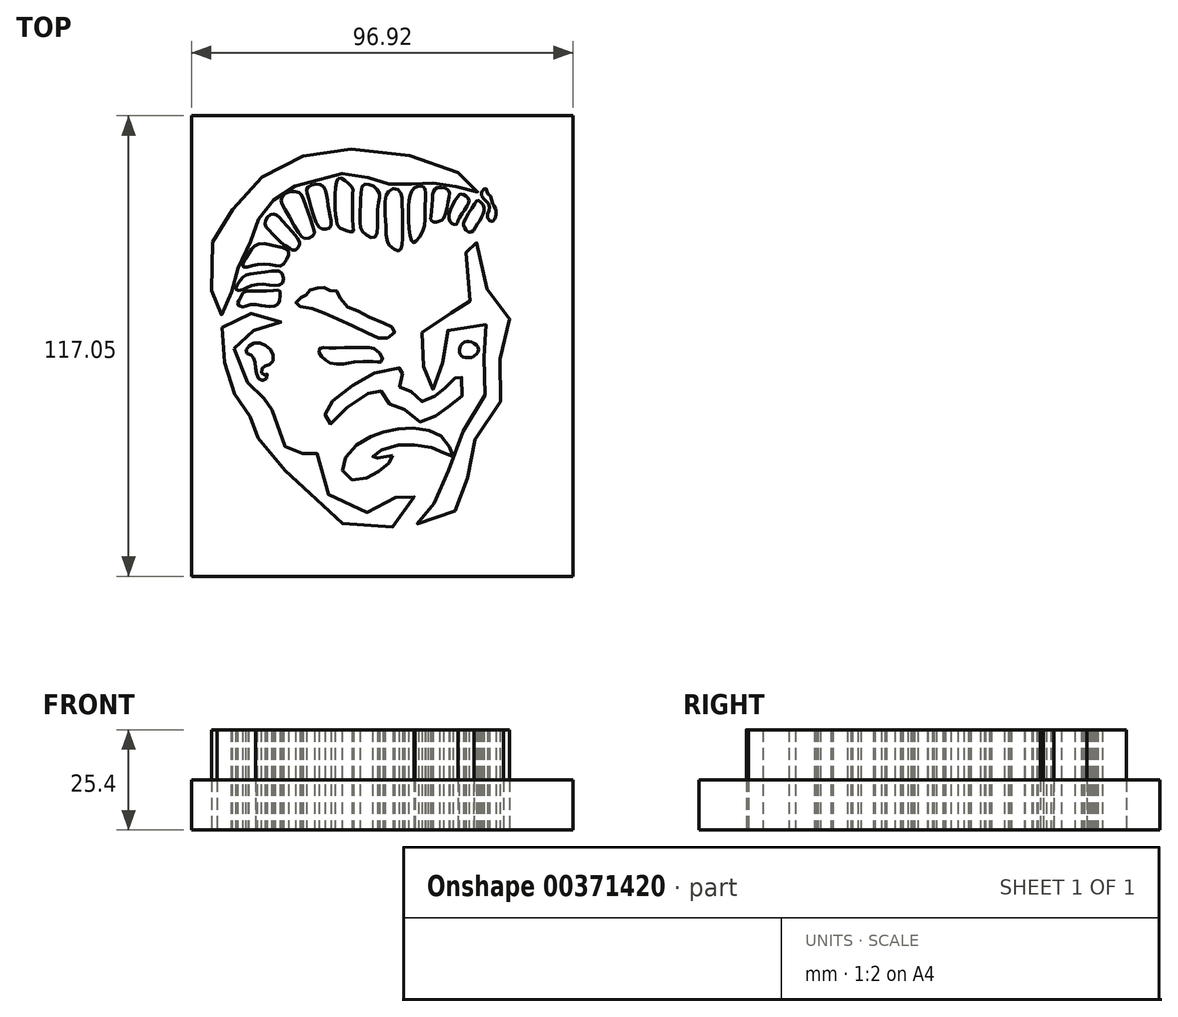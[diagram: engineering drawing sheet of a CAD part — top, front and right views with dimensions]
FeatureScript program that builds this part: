
annotation { "Feature Type Name" : "Feature", "Feature Type Description" : "" }
export const myFeature = defineFeature(function(context is Context, id is Id, definition is map)
    precondition{}
    {
        {
            var Q0;
            Q0=qCreatedBy(makeId("Top.planeOp"),FACE);
            var sketch = newSketch(context, id + "F0", { "sketchPlane" : qUnion([Q0])});
            skFitSpline(sketch, "E0", {"points": [v(-40.21, -13.64) * mm, v(-40.76, -11.92) * mm, v(-40.07, -9.65) * mm, v(-37.45, -9.1) * mm, v(-33.75, -9.1) * mm, v(-32.66, -9.45) * mm, v(-30.04, -9.1) * mm, v(-28.51, -7.42) * mm, v(-28.37, -5.7) * mm, v(-29.95, -4.51) * mm, v(-33.85, -4.26) * mm, v(-36.61, -4.8) * mm, v(-39.77, -4.9) * mm, v(-41.6, -5.4) * mm, v(-43.08, -7.87) * mm, v(-44.4, -10.93) * mm, v(-44.46, -13.94) * mm, v(-43.27, -16.46) * mm, v(-41.55, -18.43) * mm, v(-40.6, -20.46) * mm, v(-40.26, -23.12) * mm, v(-40.16, -25.64) * mm, v(-39.77, -28.9) * mm, v(-39.03, -30.77) * mm, v(-36.8, -31.07) * mm, v(-35.47, -30.57) * mm, v(-34.73, -30.43) * mm, v(-34.78, -32.06) * mm, v(-34.64, -34.38) * mm, v(-33.8, -37.24) * mm, v(-31.87, -40.2) * mm, v(-29, -43.11) * mm, v(-25.95, -45.58) * mm, v(-23.48, -47.16) * mm, v(-22, -48.05) * mm, v(-20.91, -50.57) * mm, v(-18.7, -54.07) * mm, v(-15.63, -56.59) * mm, v(-11, -58.66) * mm, v(-5.41, -59.45) * mm, v(0, -58.9) * mm, v(3.03, -57.08) * mm, v(5.1, -53.97) * mm, v(5.5, -51.45) * mm, v(4.95, -49.43) * mm, v(3.47, -48.6) * mm, v(1.94, -49.63) * mm, v(0.86, -51.3) * mm, v(0.51, -52.89) * mm, v(-0.97, -54.37) * mm, v(-4.43, -55.1) * mm, v(-8.47, -55.06) * mm, v(-13.26, -53.38) * mm, v(-15.68, -51.5) * mm, v(-17.3, -48.79) * mm, v(-18.54, -44.6) * mm, v(-19.09, -40.8) * mm, v(-19.83, -38.47) * mm, v(-21.65, -37.49) * mm, v(-22.84, -37.88) * mm, v(-22.94, -39.66) * mm, v(-22.84, -42.03) * mm, v(-23.18, -42.08) * mm, v(-24.02, -41.73) * mm, v(-25.1, -40.9) * mm, v(-28.07, -37.49) * mm, v(-30.14, -34.08) * mm, v(-30.64, -32.45) * mm, v(-30.64, -29) * mm, v(-30.04, -26.18) * mm, v(-29.95, -25.24) * mm, v(-30.49, -25.1) * mm, v(-31.58, -25.69) * mm, v(-33.65, -26.63) * mm, v(-36.31, -26.77) * mm, v(-36.61, -26.63) * mm, v(-36.61, -24.95) * mm, v(-36.96, -21.2) * mm, v(-37.3, -19.22) * mm, v(-38.78, -16.36) * mm, v(-40.21, -13.64) * mm]});
            skFitSpline(sketch, "E1", {"points": [v(-35.33, -16.06) * mm, v(-36.07, -15.17) * mm, v(-37.05, -14.73) * mm, v(-37.25, -13.99) * mm, v(-35.92, -12.5) * mm, v(-33.75, -12.21) * mm, v(-31.53, -13.3) * mm, v(-30.3, -15.47) * mm, v(-30.79, -17.35) * mm, v(-32.17, -17.89) * mm, v(-33.1, -18.58) * mm, v(-33.3, -19.76) * mm, v(-32.32, -20.3) * mm, v(-31.92, -20.01) * mm, v(-31.92, -20.85) * mm, v(-32.71, -21.64) * mm, v(-34.04, -21.2) * mm, v(-34.64, -19.47) * mm, v(-34.93, -17.44) * mm, v(-35.33, -16.06) * mm]});
            skFitSpline(sketch, "E2", {"points": [v(-12.18, -13.4) * mm, v(-16.72, -13.4) * mm, v(-18.35, -13.45) * mm, v(-18.7, -14.53) * mm, v(-17.56, -16.06) * mm, v(-15.53, -17.4) * mm, v(-12.03, -17.44) * mm, v(-10.05, -17.05) * mm, v(-4.18, -16.95) * mm, v(-3.49, -17.15) * mm, v(-2.5, -16.5) * mm, v(-4.23, -13.9) * mm, v(-6.45, -13.35) * mm, v(-12.18, -13.4) * mm]});
            skFitSpline(sketch, "E3", {"points": [v(0, -40.74) * mm, v(0, -41.58) * mm, v(-1.41, -43.06) * mm, v(-4.13, -45.24) * mm, v(-7.1, -46.62) * mm, v(-10.6, -46.86) * mm, v(-12.77, -44.5) * mm, v(-12.03, -41.58) * mm, v(-8.87, -37.93) * mm, v(-4.72, -35.6) * mm, v(-2.16, -34.72) * mm, v(1.6, -34.03) * mm, v(5.8, -33.83) * mm, v(9.94, -34.57) * mm, v(12.6, -36.1) * mm, v(14.58, -38.77) * mm, v(15.42, -40.74) * mm, v(15.02, -41.29) * mm, v(13.05, -40.1) * mm, v(9.94, -38.82) * mm, v(5, -38.08) * mm, v(0.56, -38.28) * mm, v(-4.03, -40) * mm, v(-5.02, -41.04) * mm, v(-5.07, -41.63) * mm, v(-3.88, -41.48) * mm, v(0, -40.74) * mm]});
            skFitSpline(sketch, "E4", {"points": [v(10.48, -52.99) * mm, v(9.35, -53.53) * mm, v(7.27, -54.07) * mm, v(5.8, -55.8) * mm, v(5.94, -57.72) * mm, v(8.16, -58.9) * mm, v(12.6, -57.63) * mm, v(15.32, -55.65) * mm, v(16.36, -53.58) * mm, v(16.65, -51.16) * mm, v(16.8, -49.78) * mm, v(18.68, -46.91) * mm, v(20.16, -44.54) * mm, v(20.7, -41.09) * mm, v(20.55, -37.93) * mm, v(21.64, -35.31) * mm, v(23.8, -32.65) * mm, v(26.52, -28.8) * mm, v(28.1, -24.85) * mm, v(28, -21) * mm, v(27.41, -17.6) * mm, v(27.36, -14.98) * mm, v(28.5, -11.08) * mm, v(29.39, -7.67) * mm, v(29.68, -5.75) * mm, v(28.1, -3.82) * mm, v(26.33, -2.69) * mm, v(24.4, 0) * mm, v(23.41, 5.26) * mm, v(22.72, 10.1) * mm, v(21.59, 13.01) * mm, v(19.76, 14.74) * mm, v(18.28, 15.23) * mm, v(18.18, 14.74) * mm, v(18.63, 12.91) * mm, v(18.48, 8.96) * mm, v(18.33, 4.08) * mm, v(19.22, -0.56) * mm, v(20.7, -2.83) * mm, v(21.3, -3.77) * mm, v(20.4, -4.07) * mm, v(16.6, -4.51) * mm, v(12.01, -4.86) * mm, v(9.2, -6.34) * mm, v(7.96, -8.12) * mm, v(7.52, -9.6) * mm, v(7.82, -12.4) * mm, v(8.8, -14.29) * mm, v(8.85, -16.01) * mm, v(7.52, -18.83) * mm, v(6.63, -21.5) * mm, v(7.17, -23.22) * mm, v(9.35, -24.26) * mm, v(10.33, -23.81) * mm, v(10.14, -23.07) * mm, v(10.23, -21.99) * mm, v(11.02, -20.16) * mm, v(12.06, -18.83) * mm, v(13, -15.52) * mm, v(12.11, -12.5) * mm, v(12.06, -10.14) * mm, v(13.69, -9.05) * mm, v(17.44, -8.9) * mm, v(20.95, -8.56) * mm, v(22.58, -7.62) * mm, v(24.1, -7.72) * mm, v(24.55, -8.76) * mm, v(24.4, -11.57) * mm, v(23.51, -14.33) * mm, v(23.12, -17.2) * mm, v(23.66, -20.65) * mm, v(24.1, -22.87) * mm, v(23.61, -25.1) * mm, v(21.54, -27.81) * mm, v(19.47, -30.92) * mm, v(18.08, -33.88) * mm, v(17.59, -37.29) * mm, v(17.3, -39.76) * mm, v(15.12, -43.36) * mm, v(13.5, -46.17) * mm, v(13, -49.33) * mm, v(11.96, -51.7) * mm, v(10.48, -52.99) * mm]});
            skFitSpline(sketch, "E5", {"points": [v(17.5, -15.47) * mm, v(16.95, -13.99) * mm, v(17.64, -12.46) * mm, v(19.07, -11.82) * mm, v(21.04, -12.5) * mm, v(21.83, -14.14) * mm, v(20.26, -15.77) * mm, v(18.82, -15.86) * mm, v(17.5, -15.47) * mm]});
            skFitSpline(sketch, "E6", {"points": [v(13.3, -23.61) * mm, v(14.97, -22.68) * mm, v(15.91, -21.1) * mm, v(16.26, -19.81) * mm, v(16.9, -19.86) * mm, v(18.03, -22.63) * mm, v(17.89, -25.24) * mm, v(15.91, -27.42) * mm, v(13.69, -28.55) * mm, v(11.91, -29.54) * mm, v(10.48, -31.27) * mm, v(7.91, -32.5) * mm, v(5.35, -31.12) * mm, v(2.93, -28.95) * mm, v(1.6, -27.96) * mm, v(-1.22, -27.51) * mm, v(-2.4, -26.18) * mm, v(-3.14, -24) * mm, v(-4.38, -24.2) * mm, v(-7.14, -25.54) * mm, v(-11.83, -28.75) * mm, v(-15.29, -32.35) * mm, v(-16.22, -32.85) * mm, v(-16.87, -31.71) * mm, v(-17.11, -29.93) * mm, v(-16.77, -28.65) * mm, v(-14, -25.93) * mm, v(-9.66, -22.63) * mm, v(-4.92, -19.96) * mm, v(0.7, -18.73) * mm, v(2.83, -18.53) * mm, v(3.03, -19.02) * mm, v(2.53, -19.91) * mm, v(2, -20.7) * mm, v(1.7, -22.68) * mm, v(2.24, -24.16) * mm, v(3.72, -24.4) * mm, v(5.25, -24.8) * mm, v(6.63, -26.38) * mm, v(8.06, -27.22) * mm, v(9.6, -26.53) * mm, v(11.17, -25.24) * mm, v(12.16, -24.26) * mm, v(13.3, -23.61) * mm]});
            skFitSpline(sketch, "E7", {"points": [v(-6, -5.55) * mm, v(-0.77, -7.72) * mm, v(0, -8.36) * mm, v(0.51, -9.3) * mm, v(-0.72, -10.63) * mm, v(-2.7, -11.13) * mm, v(-5.76, -10) * mm, v(-12.03, -6.98) * mm, v(-17.8, -4.41) * mm, v(-21.7, -3.13) * mm, v(-24.52, -2.59) * mm, v(-24.42, -1.75) * mm, v(-23.28, -0.76) * mm, v(-22.84, 0) * mm, v(-21.65, 0) * mm, v(-21.06, 1.16) * mm, v(-19.48, 1.6) * mm, v(-18.35, 2.25) * mm, v(-16.87, 1.56) * mm, v(-15.78, 1.12) * mm, v(-14.6, 1.21) * mm, v(-13.7, 0.47) * mm, v(-12.47, -2.3) * mm, v(-9.51, -3.77) * mm, v(-6, -5.55) * mm]});
            skFitSpline(sketch, "E8", {"points": [v(-40.95, 0.72) * mm, v(-40.9, -2) * mm, v(-42.09, -4.02) * mm, v(-43.42, -4.86) * mm, v(-43.62, -5.7) * mm, v(-44.95, -5.15) * mm, v(-45.94, 0) * mm, v(-45.8, 6.94) * mm, v(-45.7, 13.75) * mm, v(-45.2, 15.73) * mm, v(-41.7, 20.37) * mm, v(-37.3, 26) * mm, v(-33.7, 29.45) * mm, v(-30, 32.21) * mm, v(-22.94, 35.22) * mm, v(-15.43, 36.85) * mm, v(-8.77, 37) * mm, v(1.84, 35.97) * mm, v(12.11, 33.2) * mm, v(17.2, 30.88) * mm, v(20.9, 28.7) * mm, v(22.23, 27.38) * mm, v(21.3, 26.04) * mm, v(20.4, 26.78) * mm, v(19.22, 27.33) * mm, v(16.95, 27.43) * mm, v(15.12, 27.82) * mm, v(13.64, 28.7) * mm, v(11.62, 28.8) * mm, v(10.04, 28.36) * mm, v(8.26, 28.46) * mm, v(6.83, 28.86) * mm, v(5.5, 28.56) * mm, v(4.31, 27.97) * mm, v(2.53, 27.82) * mm, v(1.4, 28.31) * mm, v(-0.48, 28.41) * mm, v(-1.76, 27.82) * mm, v(-3.49, 28.12) * mm, v(-4.62, 29.15) * mm, v(-6.3, 29.84) * mm, v(-8.18, 29.8) * mm, v(-9.9, 29.94) * mm, v(-12.27, 30.73) * mm, v(-14.8, 30.83) * mm, v(-15.83, 29.6) * mm, v(-17.56, 29.25) * mm, v(-19.43, 29.45) * mm, v(-21.9, 29) * mm, v(-22.84, 28.12) * mm, v(-25.2, 27.72) * mm, v(-27.48, 27.28) * mm, v(-29.6, 25.55) * mm, v(-30.24, 24.07) * mm, v(-30.69, 22.98) * mm, v(-32.07, 21.8) * mm, v(-33.55, 20.17) * mm, v(-34.34, 18.4) * mm, v(-34.39, 16.22) * mm, v(-34.98, 14.54) * mm, v(-36.31, 13.46) * mm, v(-38.14, 11.14) * mm, v(-39.13, 8.67) * mm, v(-39.32, 6.15) * mm, v(-39.77, 4.72) * mm, v(-40.76, 2.84) * mm, v(-40.95, 0.72) * mm]});
            skFitSpline(sketch, "E9", {"points": [v(-38.98, -1.35) * mm, v(-38.04, 0.52) * mm, v(-35.82, 1.02) * mm, v(-30.3, 1.12) * mm, v(-28.71, 1.12) * mm, v(-28.61, -0.71) * mm, v(-29.3, -2.44) * mm, v(-31.48, -2.93) * mm, v(-33.5, -2.64) * mm, v(-36.61, -2.54) * mm, v(-38.34, -3.03) * mm, v(-39.32, -2.3) * mm, v(-38.98, -1.35) * mm]});
            skFitSpline(sketch, "E10", {"points": [v(-36.99, 1.91) * mm, v(-38.73, 1.22) * mm, v(-39.84, 1.53) * mm, v(-38.97, 3.34) * mm, v(-37.65, 4.9) * mm, v(-36.23, 5.39) * mm, v(-31.09, 6.01) * mm, v(-29.32, 6.15) * mm, v(-28.38, 5.8) * mm, v(-27.75, 3.68) * mm, v(-28.66, 2.54) * mm, v(-30.88, 2.54) * mm, v(-34.32, 2.71) * mm, v(-36.99, 1.91) * mm]});
            skFitSpline(sketch, "E11", {"points": [v(-34.25, 7.78) * mm, v(-36.88, 7.16) * mm, v(-38.13, 7.33) * mm, v(-36.6, 10.39) * mm, v(-35.43, 12.23) * mm, v(-33.3, 13.1) * mm, v(-29.18, 12.33) * mm, v(-27.16, 11.8) * mm, v(-26.4, 10.87) * mm, v(-26.92, 9.1) * mm, v(-28.34, 7.43) * mm, v(-30.43, 7.64) * mm, v(-34.25, 7.78) * mm]});
            skFitSpline(sketch, "E12", {"points": [v(-31.4, 16.5) * mm, v(-32.4, 17.89) * mm, v(-31.95, 19.59) * mm, v(-30.67, 20.52) * mm, v(-29.42, 20.28) * mm, v(-27.48, 18.34) * mm, v(-23.66, 13.55) * mm, v(-23.7, 12.57) * mm, v(-24.66, 11.4) * mm, v(-26.05, 11.8) * mm, v(-28.34, 13.4) * mm, v(-31.4, 16.5) * mm]});
            skFitSpline(sketch, "E13", {"points": [v(-23.9, 15.87) * mm, v(-27.72, 22.43) * mm, v(-28.3, 23.96) * mm, v(-27.61, 25.52) * mm, v(-25.29, 26.36) * mm, v(-23.55, 25.9) * mm, v(-22.65, 24.3) * mm, v(-21.09, 20.04) * mm, v(-19.98, 16.36) * mm, v(-19.84, 15.6) * mm, v(-20.84, 14.66) * mm, v(-22.62, 14.45) * mm, v(-23.9, 15.87) * mm]});
            skFitSpline(sketch, "E14", {"points": [v(-19.39, 18.4) * mm, v(-21.64, 25.84) * mm, v(-21.71, 27.22) * mm, v(-19.94, 28.16) * mm, v(-17.79, 27.78) * mm, v(-16.78, 25.42) * mm, v(-16.2, 21.95) * mm, v(-15.64, 18.65) * mm, v(-16.05, 17.05) * mm, v(-17.72, 16.77) * mm, v(-19.39, 18.4) * mm]});
            skFitSpline(sketch, "E15", {"points": [v(-14.63, 23.65) * mm, v(-14.25, 28.75) * mm, v(-13.38, 29.72) * mm, v(-11.57, 28.61) * mm, v(-10.19, 27.22) * mm, v(-10.19, 24.97) * mm, v(-9.98, 16.98) * mm, v(-10.15, 16.08) * mm, v(-13.41, 17.12) * mm, v(-14.32, 19.2) * mm, v(-14.63, 23.65) * mm]});
            skFitSpline(sketch, "E16", {"points": [v(-8.31, 21.4) * mm, v(-8.24, 18.27) * mm, v(-7.79, 16.22) * mm, v(-5.67, 14.73) * mm, v(-4.28, 14.86) * mm, v(-3.83, 18.82) * mm, v(-3.52, 24.03) * mm, v(-3.31, 25.66) * mm, v(-4.46, 27.3) * mm, v(-6.3, 28.2) * mm, v(-7.62, 27.82) * mm, v(-8.07, 24.48) * mm, v(-8.31, 21.4) * mm]});
            skFitSpline(sketch, "E17", {"points": [v(-1.92, 20.35) * mm, v(-1.85, 23.96) * mm, v(-1.26, 26.04) * mm, v(0.5, 27.12) * mm, v(2.07, 25.98) * mm, v(2.42, 24.2) * mm, v(2.56, 19.2) * mm, v(2.45, 13.72) * mm, v(2.24, 11.91) * mm, v(1.48, 11.22) * mm, v(-0.3, 12.2) * mm, v(-1.3, 13.4) * mm, v(-1.75, 17.92) * mm, v(-1.92, 20.35) * mm]});
            skFitSpline(sketch, "E18", {"points": [v(4.12, 22.6) * mm, v(4.5, 25.56) * mm, v(5.75, 27.36) * mm, v(7.87, 27.47) * mm, v(8.36, 26.22) * mm, v(8.25, 21.6) * mm, v(7.87, 16.8) * mm, v(5.82, 13.58) * mm, v(5.13, 13.34) * mm, v(4.22, 16.18) * mm, v(4.12, 22.6) * mm]});
            skFitSpline(sketch, "E19", {"points": [v(9.74, 20.07) * mm, v(10.16, 25.14) * mm, v(10.61, 26.7) * mm, v(12.1, 27.36) * mm, v(14.26, 26.53) * mm, v(14.22, 24.27) * mm, v(13.08, 19.62) * mm, v(12.07, 18.79) * mm, v(10.54, 18.51) * mm, v(9.78, 19.03) * mm, v(9.74, 20.07) * mm]});
            skFitSpline(sketch, "E20", {"points": [v(14.4, 20.52) * mm, v(16.72, 25.21) * mm, v(17.66, 25.63) * mm, v(19.3, 24.48) * mm, v(19.05, 22.78) * mm, v(16.72, 19.14) * mm, v(16.38, 18.16) * mm, v(15.2, 18.06) * mm, v(14.4, 20.52) * mm]});
            skFitSpline(sketch, "E21", {"points": [v(18.15, 18.68) * mm, v(20.96, 23.34) * mm, v(21.9, 24) * mm, v(23.18, 22.5) * mm, v(22.9, 20.35) * mm, v(21.44, 17.82) * mm, v(19.78, 15.94) * mm, v(18.5, 16.8) * mm, v(17.97, 18.02) * mm, v(18.15, 18.68) * mm]});
            skFitSpline(sketch, "E22", {"points": [v(24.36, 23.23) * mm, v(22.97, 24.66) * mm, v(22.66, 26.22) * mm, v(23.74, 27.09) * mm, v(24.05, 25.98) * mm, v(24.92, 24.97) * mm, v(25.47, 23.1) * mm, v(26.13, 21.88) * mm, v(26.3, 20.6) * mm, v(25.37, 18.72) * mm, v(24.12, 19.55) * mm, v(24.5, 21.5) * mm, v(24.36, 23.23) * mm]});
            skSolve(sketch);
        }
        {
            var Q0;
            Q0 = qSketchRegion(id + "F0", true);
            extrude(context, id + "F1", {"entities" : qUnion([Q0]), "depth" : 25.4 * mm});
        }
        {
            var Q0;
            Q0=qCreatedBy(makeId("Top.planeOp"),FACE);
            var sketch = newSketch(context, id + "F2", { "sketchPlane" : qUnion([Q0])});
            skLineSegment(sketch, "E23.bottom", {"start": v(45.87, 45.57) * mm, "end": v(-51.05, 45.57) * mm});
            skLineSegment(sketch, "E23.top", {"start": v(45.87, -71.48) * mm, "end": v(-51.05, -71.48) * mm});
            skLineSegment(sketch, "E23.left", {"start": v(45.87, 45.57) * mm, "end": v(45.87, -71.48) * mm});
            skLineSegment(sketch, "E23.right", {"start": v(-51.05, 45.57) * mm, "end": v(-51.05, -71.48) * mm});
            skPoint(sketch, "E23.middle", {"position": v(-2.6, -12.95) * mm});
            skSolve(sketch);
        }
        {
            var Q0;
            Q0 = qSketchRegion(id + "F2", true);
            extrude(context, id + "F3", {"entities" : qUnion([Q0]), "depth" : 12.7 * mm});
        }
    });
